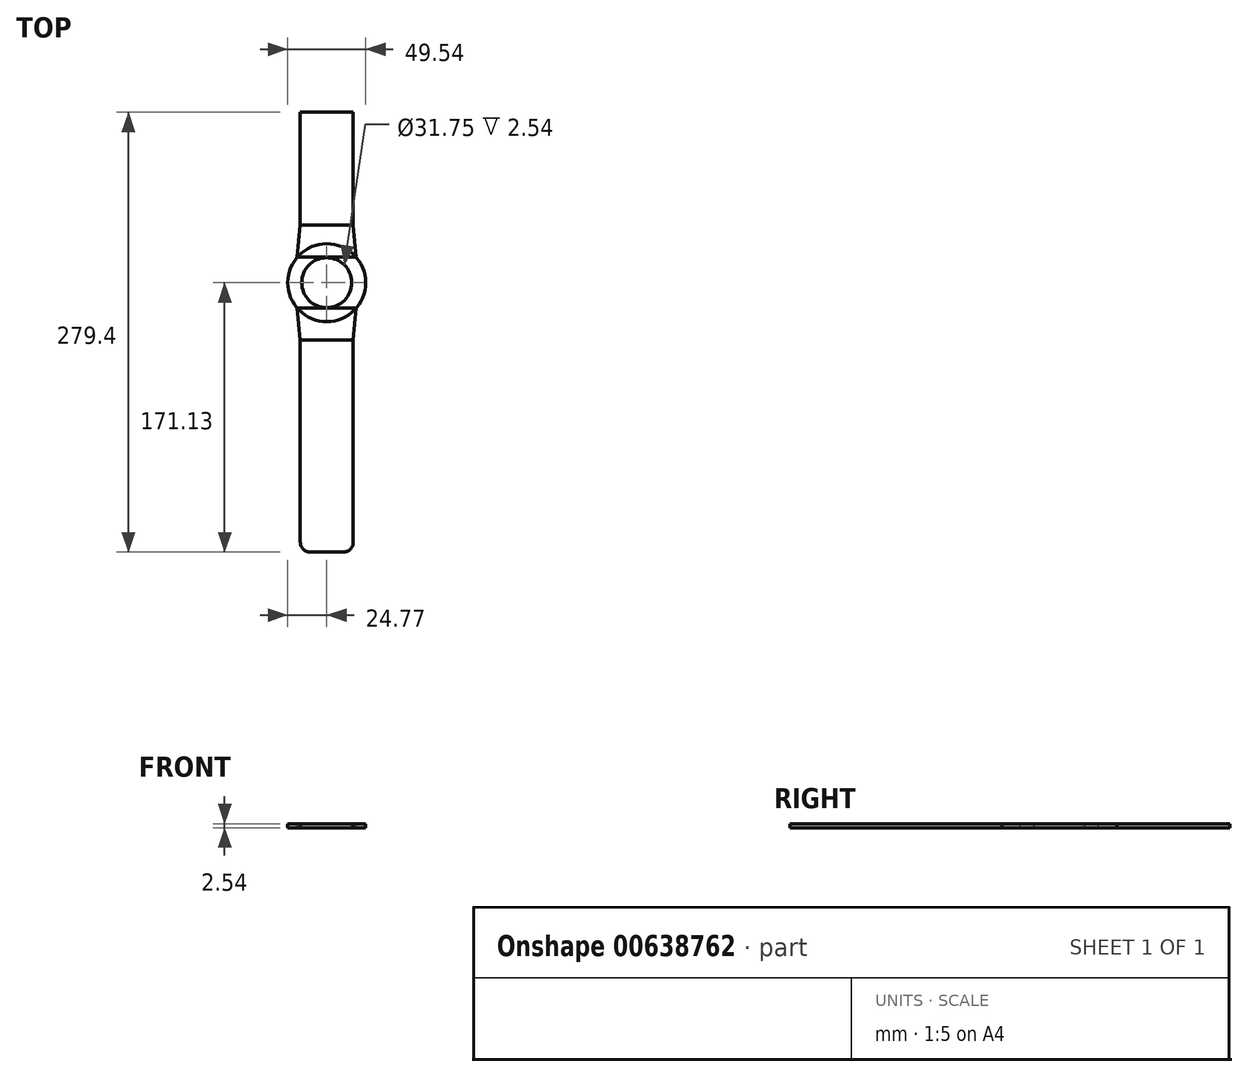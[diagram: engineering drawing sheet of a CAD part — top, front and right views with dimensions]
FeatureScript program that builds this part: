
annotation { "Feature Type Name" : "Feature", "Feature Type Description" : "" }
export const myFeature = defineFeature(function(context is Context, id is Id, definition is map)
    precondition{}
    {
        {
            var Q0;
            Q0=qCreatedBy(makeId("Top.planeOp"),FACE);
            var sketch = newSketch(context, id + "F0", { "sketchPlane" : qUnion([Q0])});
            skCircle(sketch, "E0", {"center": v(0, 0) * mm, "radius": 15.88 * mm});
            skCircle(sketch, "E1", {"center": v(0, 0) * mm, "radius": 24.77 * mm});
            skSolve(sketch);
        }
        {
            var Q0;
            Q0=qCreatedBy(makeId("Top.planeOp"),FACE);
            var sketch = newSketch(context, id + "F1", { "sketchPlane" : qUnion([Q0])});
            skLineSegment(sketch, "E2.bottom", {"start": v(-18.73, 36.51) * mm, "end": v(18.73, 36.51) * mm});
            skLineSegment(sketch, "E2.top", {"start": v(-18.73, -36.51) * mm, "end": v(18.73, -36.51) * mm});
            skLineSegment(sketch, "E2.left", {"start": v(-18.73, 36.51) * mm, "end": v(-18.73, -36.51) * mm});
            skLineSegment(sketch, "E2.right", {"start": v(18.73, 36.51) * mm, "end": v(18.73, -36.51) * mm});
            skPoint(sketch, "E2.middle", {"position": v(0, 0) * mm});
            skLineSegment(sketch, "E3.bottom", {"start": v(-16.83, 36.51) * mm, "end": v(16.83, 36.51) * mm});
            skLineSegment(sketch, "E3.top", {"start": v(-16.83, -36.51) * mm, "end": v(16.83, -36.51) * mm});
            skLineSegment(sketch, "E3.left", {"start": v(-16.83, 36.51) * mm, "end": v(-16.83, -36.51) * mm});
            skLineSegment(sketch, "E3.right", {"start": v(16.83, 36.51) * mm, "end": v(16.83, -36.51) * mm});
            skSolve(sketch);
        }
        {
            var Q0;
            Q0=qCreatedBy(makeId("Top.planeOp"),FACE);
            var sketch = newSketch(context, id + "F2", { "sketchPlane" : qUnion([Q0])});
            skPoint(sketch, "E4", {"position": v(-18.73, 16.18) * mm});
            skPoint(sketch, "E5", {"position": v(-18.73, -16.18) * mm});
            skPoint(sketch, "E6", {"position": v(18.73, -16.18) * mm});
            skPoint(sketch, "E7", {"position": v(18.73, 16.18) * mm});
            skSolve(sketch);
        }
        {
            var Q0;
            Q0=qCreatedBy(makeId("Top.planeOp"),FACE);
            var sketch = newSketch(context, id + "F3", { "sketchPlane" : qUnion([Q0])});
            skLineSegment(sketch, "E8", {"start": v(-18.73, -16.18) * mm, "end": v(-16.83, -36.51) * mm});
            skLineSegment(sketch, "E9", {"start": v(-16.83, -36.51) * mm, "end": v(16.83, -36.51) * mm});
            skLineSegment(sketch, "E10", {"start": v(16.83, -36.51) * mm, "end": v(18.73, -16.18) * mm});
            skLineSegment(sketch, "E11", {"start": v(-18.73, 16.18) * mm, "end": v(-16.83, 36.51) * mm});
            skLineSegment(sketch, "E12", {"start": v(-16.83, 36.51) * mm, "end": v(16.83, 36.51) * mm});
            skLineSegment(sketch, "E13", {"start": v(16.83, 36.51) * mm, "end": v(18.73, 16.18) * mm});
            skLineSegment(sketch, "E14", {"start": v(-18.73, 16.18) * mm, "end": v(18.73, 16.18) * mm});
            skLineSegment(sketch, "E15", {"start": v(-18.73, -16.18) * mm, "end": v(18.73, -16.18) * mm});
            skSolve(sketch);
        }
        {
            var Q0;
            Q0=qCreatedBy(makeId("Top.planeOp"),FACE);
            var sketch = newSketch(context, id + "F4", { "sketchPlane" : qUnion([Q0])});
            skLineSegment(sketch, "E16.bottom", {"start": v(-16.77, -36.51) * mm, "end": v(16.89, -36.51) * mm});
            skLineSegment(sketch, "E16.top", {"start": v(-10.42, -171.13) * mm, "end": v(10.54, -171.13) * mm});
            skLineSegment(sketch, "E16.left", {"start": v(-16.77, -36.51) * mm, "end": v(-16.77, -164.78) * mm});
            skLineSegment(sketch, "E16.right", {"start": v(16.89, -36.51) * mm, "end": v(16.89, -164.78) * mm});
            skPoint(sketch, "E17.visualSharp", {"position": v(-16.77, -171.13) * mm});
            skArc(sketch, "E17.filletArc", {"start": v(-16.77, -164.78) * mm, "mid": v(-14.9, -169.27) * mm, "end": v(-10.42, -171.13) * mm});
            skPoint(sketch, "E18.visualSharp", {"position": v(16.89, -171.13) * mm});
            skArc(sketch, "E18.filletArc", {"start": v(10.54, -171.13) * mm, "mid": v(15.03, -169.27) * mm, "end": v(16.89, -164.78) * mm});
            skSolve(sketch);
        }
        {
            var Q0;
            Q0=qCreatedBy(makeId("Top.planeOp"),FACE);
            var sketch = newSketch(context, id + "F5", { "sketchPlane" : qUnion([Q0])});
            skLineSegment(sketch, "E19.bottom", {"start": v(-16.83, 36.51) * mm, "end": v(16.83, 36.51) * mm});
            skLineSegment(sketch, "E19.top", {"start": v(-16.83, 108.27) * mm, "end": v(16.83, 108.27) * mm});
            skLineSegment(sketch, "E19.left", {"start": v(-16.83, 36.51) * mm, "end": v(-16.83, 108.27) * mm});
            skLineSegment(sketch, "E19.right", {"start": v(16.83, 36.51) * mm, "end": v(16.83, 108.27) * mm});
            skSolve(sketch);
        }
        {
            var Q0;
            Q0=makeQuery(id+"F0.imprint","IMPRINT",FACE,{"disambiguationData":[TD([[makeQuery(id+"F0.imprint","IMPRINT",EDGE,{"derivedFrom":sQuery(id+"F0.wireOp",EDGE,"E0")}),-1.0]])]});
            var Q1;
            Q1=makeQuery(id+"F3.imprint","IMPRINT",FACE,{"disambiguationData":[TD([[makeQuery(id+"F3.imprint","IMPRINT",EDGE,{"derivedFrom":sQuery(id+"F3.wireOp",EDGE,"E8")}),1.0]])]});
            var Q2;
            Q2=makeQuery(id+"F3.imprint","IMPRINT",FACE,{"disambiguationData":[TD([[makeQuery(id+"F3.imprint","IMPRINT",EDGE,{"derivedFrom":sQuery(id+"F3.wireOp",EDGE,"E11")}),-1.0]])]});
            var Q3;
            Q3=makeQuery(id+"F4.imprint","IMPRINT",FACE,{"disambiguationData":[TD([[makeQuery(id+"F4.imprint","IMPRINT",EDGE,{"derivedFrom":sQuery(id+"F4.wireOp",EDGE,"E16.bottom")}),-1.0]])]});
            var Q4;
            Q4=makeQuery(id+"F5.imprint","IMPRINT",FACE,{"disambiguationData":[TD([[makeQuery(id+"F5.imprint","IMPRINT",EDGE,{"derivedFrom":sQuery(id+"F5.wireOp",EDGE,"E19.bottom")}),1.0]])]});
            extrude(context, id + "F6", {"entities" : qUnion([Q0, Q1, Q2, Q3, Q4]), "oppositeDirection" : true, "depth" : 2.54 * mm, "offsetDistance" : 25.4 * mm});
        }
    });
